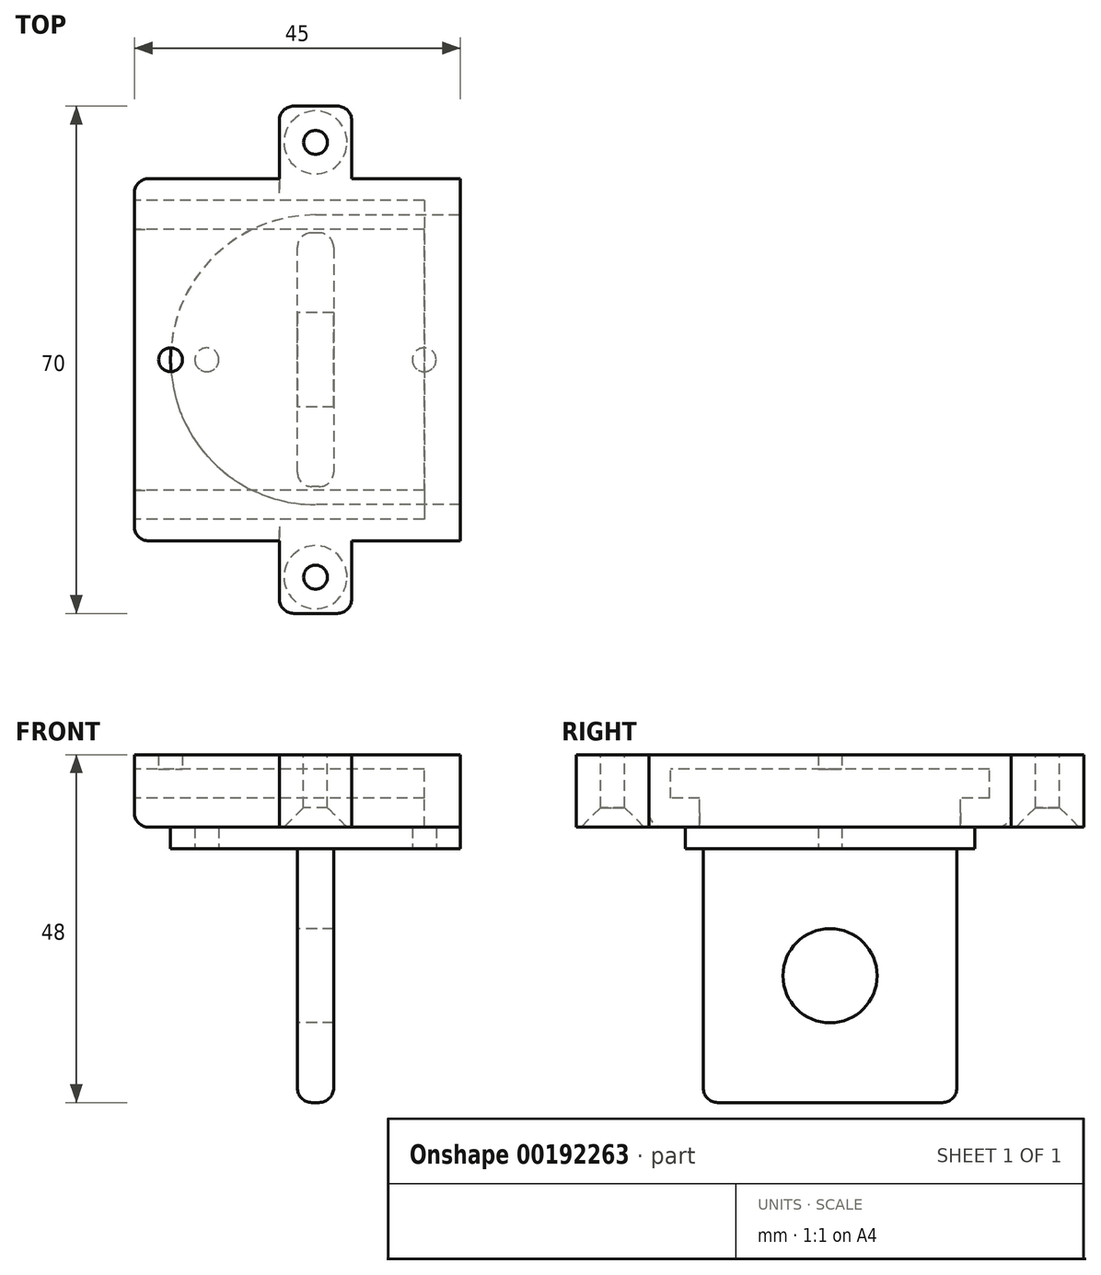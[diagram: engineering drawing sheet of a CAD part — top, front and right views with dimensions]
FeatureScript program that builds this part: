
annotation { "Feature Type Name" : "Feature", "Feature Type Description" : "" }
export const myFeature = defineFeature(function(context is Context, id is Id, definition is map)
    precondition{}
    {
        {
            var Q0;
            Q0=qCreatedBy(makeId("Right.planeOp"),FACE);
            var sketch = newSketch(context, id + "F0", { "sketchPlane" : qUnion([Q0])});
            skLineSegment(sketch, "E0", {"start": v(0, 0) * mm, "end": v(0, 35) * mm});
            skLineSegment(sketch, "E1", {"start": v(0, 35) * mm, "end": v(35, 35) * mm});
            skLineSegment(sketch, "E2", {"start": v(35, 35) * mm, "end": v(35, 0) * mm});
            skLineSegment(sketch, "E3", {"start": v(35, 0) * mm, "end": v(0, 0) * mm});
            skLineSegment(sketch, "E4", {"start": v(17.5, 35) * mm, "end": v(17.5, 0) * mm});
            skCircle(sketch, "E5", {"center": v(17.5, 17.5) * mm, "radius": 6.5 * mm});
            skSolve(sketch);
        }
        {
            var Q0;
            Q0 = qSketchRegion(id + "F0", true);
            var Q1;
            {var subQ6=sQuery(id+"F0.wireOp",EDGE,"E2");Q1=makeQuery(id+"F0.imprint","IMPRINT",FACE,{"disambiguationData":[TD([[makeQuery(id+"F0.imprint","IMPRINT",EDGE,{"derivedFrom":subQ6}),-1.0]])]});}
            extrude(context, id + "F1", {"entities" : qUnion([Q0, Q1]), "depth" : 5 * mm});
        }
        {
            var Q0;
            Q0=makeQuery(id+"F1.opExtrude","SWEPT_FACE",FACE,{"disambiguationData":[OSD([sQuery(id+"F0.wireOp",EDGE,"E1")])]});
            var sketch = newSketch(context, id + "F2", { "sketchPlane" : qUnion([Q0])});
            skLineSegment(sketch, "E6", {"start": v(0, 17.5) * mm, "end": v(5, 17.5) * mm});
            skCircle(sketch, "E7", {"center": v(2.5, 17.5) * mm, "radius": 20 * mm});
            skLineSegment(sketch, "E8", {"start": v(2.5, 17.5) * mm, "end": v(-17.5, 17.5) * mm});
            skLineSegment(sketch, "E9", {"start": v(-17.5, 17.5) * mm, "end": v(-17.5, 37.5) * mm});
            skLineSegment(sketch, "E10", {"start": v(-17.5, 37.5) * mm, "end": v(2.5, 37.5) * mm});
            skLineSegment(sketch, "E11", {"start": v(2.5, 37.5) * mm, "end": v(22.5, 37.5) * mm});
            skLineSegment(sketch, "E12", {"start": v(22.5, 37.5) * mm, "end": v(22.5, -2.5) * mm});
            skLineSegment(sketch, "E13", {"start": v(22.5, -2.5) * mm, "end": v(-17.5, -2.5) * mm});
            skLineSegment(sketch, "E14", {"start": v(-17.5, -2.5) * mm, "end": v(-17.5, 17.5) * mm});
            skSolve(sketch);
        }
        {
            var Q0;
            Q0=makeQuery(id+"F2.imprint","IMPRINT",FACE,{"disambiguationData":[TD([[makeQuery(id+"F2.imprint","IMPRINT",EDGE,{"derivedFrom":sQuery(id+"F2.wireOp",EDGE,"E7")}),1.0]])]});
            var Q1;
            {var subQ0=sQuery(id+"F2.wireOp",EDGE,"E6");Q1=makeQuery(id+"F2.imprint","IMPRINT",FACE,{"disambiguationData":[TD([[makeQuery(id+"F2.imprint","IMPRINT",EDGE,{"derivedFrom":subQ0}),1.0]])]});}
            var Q2;
            {var subQ0=sQuery(id+"F2.wireOp",EDGE,"E6");Q2=makeQuery(id+"F2.imprint","IMPRINT",FACE,{"disambiguationData":[TD([[makeQuery(id+"F2.imprint","IMPRINT",EDGE,{"derivedFrom":subQ0}),-1.0]])]});}
            var Q3;
            {var subQ0=sQuery(id+"F2.wireOp",EDGE,"E11");Q3=makeQuery(id+"F2.imprint","IMPRINT",FACE,{"disambiguationData":[TD([[makeQuery(id+"F2.imprint","IMPRINT",EDGE,{"derivedFrom":subQ0}),-1.0]])]});}
            var Q4;
            {var subQ0=sQuery(id+"F2.wireOp",EDGE,"E12");var subQ1=sQuery(id+"F2.wireOp",EDGE,"E7");var subQ2=makeQuery(id+"F2.imprint","INTERSECT",VERTEX,{"derivedFrom":[subQ1,subQ0]});Q4=makeQuery(id+"F2.imprint","IMPRINT",FACE,{"disambiguationData":[TD([[makeQuery(id+"F2.imprint","IMPRINT",EDGE,{"disambiguationData":[TD([[subQ2,1.0]])],"derivedFrom":subQ1}),-1.0]])]});}
            extrude(context, id + "F3", {"entities" : qUnion([Q0, Q1, Q2, Q3, Q4]), "operationType" : NewBodyOperationType.ADD, "depth" : 3 * mm});
        }
        {
            var Q0;
            Q0=makeQuery(id+"F3.opExtrude","CAP_FACE",FACE,{"disambiguationData":[OSD([sQuery(id+"F2.wireOp",EDGE,"E7")])],"isStart":false});
            var sketch = newSketch(context, id + "F4", { "sketchPlane" : qUnion([Q0])});
            skLineSegment(sketch, "E15", {"start": v(2.5, 17.5) * mm, "end": v(-17.5, 17.5) * mm});
            skLineSegment(sketch, "E16", {"start": v(-17.5, 17.5) * mm, "end": v(-12.5, 17.5) * mm});
            skLineSegment(sketch, "E17", {"start": v(2.5, 17.5) * mm, "end": v(2.5, 32.5) * mm});
            skLineSegment(sketch, "E18", {"start": v(2.5, 17.5) * mm, "end": v(17.5, 17.5) * mm});
            skSolve(sketch);
        }
        {
            var Q0;
            Q0=sQuery(id+"F4.wireOp",VERTEX,"E16.end");
            var Q1;
            Q1=sQuery(id+"F4.wireOp",VERTEX,"E18.end");
            var Q2;
            Q2=makeQuery(id+"F1.opExtrude","SWEPT_BODY",BODY,{"disambiguationData":[OSD([sQuery(id+"F0.wireOp",EDGE,"E0"),sQuery(id+"F0.wireOp",EDGE,"E1"),sQuery(id+"F0.wireOp",EDGE,"E2"),sQuery(id+"F0.wireOp",EDGE,"E3"),sQuery(id+"F0.wireOp",EDGE,"E5")])]});
            hole(context, id + "F5", {"style" : HoleStyle.SIMPLE, "endStyle" : HoleEndStyle.THROUGH, "holeDiameter" : 3.3 * mm, "locations" : qUnion([Q0, Q1]), "scope" : qUnion([Q2]), "isTappedThrough" : true, "startStyle" : HoleStartStyle.PART});
        }
        {
            var Q0;
            Q0=makeQuery(id+"F3.opExtrude","CAP_FACE",FACE,{"disambiguationData":[OSD([sQuery(id+"F2.wireOp",EDGE,"E7")])],"isStart":false});
            var sketch = newSketch(context, id + "F6", { "sketchPlane" : qUnion([Q0])});
            skLineSegment(sketch, "E19", {"start": v(2.5, 17.5) * mm, "end": v(2.5, 42.5) * mm});
            skLineSegment(sketch, "E20", {"start": v(2.5, 42.5) * mm, "end": v(22.5, 42.5) * mm});
            skLineSegment(sketch, "E21", {"start": v(22.5, 42.5) * mm, "end": v(22.5, -7.5) * mm});
            skLineSegment(sketch, "E22", {"start": v(22.5, -7.5) * mm, "end": v(-22.5, -7.5) * mm});
            skLineSegment(sketch, "E23", {"start": v(-22.5, -7.5) * mm, "end": v(-22.5, 42.5) * mm});
            skLineSegment(sketch, "E24", {"start": v(-22.5, 42.5) * mm, "end": v(2.5, 42.5) * mm});
            skLineSegment(sketch, "E25", {"start": v(2.5, 42.5) * mm, "end": v(-2.5, 42.5) * mm});
            skLineSegment(sketch, "E26", {"start": v(2.5, 17.5) * mm, "end": v(4.5, 17.5) * mm});
            skLineSegment(sketch, "E27.MirrorCS", {"start": v(5.33, -17.5) * mm, "end": v(5.33, -7.5) * mm});
            skLineSegment(sketch, "E28", {"start": v(-2.5, 42.5) * mm, "end": v(-2.5, 52.5) * mm});
            skLineSegment(sketch, "E29", {"start": v(-2.5, 52.5) * mm, "end": v(7.5, 52.5) * mm});
            skLineSegment(sketch, "E30", {"start": v(7.5, 52.5) * mm, "end": v(7.5, 42.5) * mm});
            skLineSegment(sketch, "E31.MirrorCS", {"start": v(-2.5, -17.5) * mm, "end": v(7.5, -17.5) * mm});
            skLineSegment(sketch, "E32.MirrorCS", {"start": v(7.5, -17.5) * mm, "end": v(7.5, -7.5) * mm});
            skLineSegment(sketch, "E33.MirrorCS", {"start": v(-2.5, -7.5) * mm, "end": v(-2.5, -17.5) * mm});
            skSolve(sketch);
        }
        {
            var Q0;
            Q0 = qSketchRegion(id + "F6", true);
            extrude(context, id + "F7", {"entities" : qUnion([Q0]), "depth" : 10 * mm});
        }
        {
            var Q0;
            Q0=makeQuery(id+"F7.opExtrude","SWEPT_FACE",FACE,{"disambiguationData":[OSD([sQuery(id+"F6.wireOp",EDGE,"E23")])]});
            var sketch = newSketch(context, id + "F8", { "sketchPlane" : qUnion([Q0])});
            skLineSegment(sketch, "E34", {"start": v(-42.5, 38) * mm, "end": v(-42.5, 42) * mm});
            skLineSegment(sketch, "E35", {"start": v(-42.5, 42) * mm, "end": v(7.5, 42) * mm});
            skPoint(sketch, "E35.endSnap0", {"position": v(7.5, 43) * mm});
            skLineSegment(sketch, "E36", {"start": v(7.5, 42) * mm, "end": v(7.5, 48) * mm});
            skLineSegment(sketch, "E37", {"start": v(7.5, 48) * mm, "end": v(-42.5, 48) * mm});
            skLineSegment(sketch, "E38", {"start": v(-42.5, 48) * mm, "end": v(-42.5, 42) * mm});
            skLineSegment(sketch, "E39", {"start": v(-42.5, 42) * mm, "end": v(-39.5, 42) * mm});
            skLineSegment(sketch, "E40", {"start": v(7.5, 42) * mm, "end": v(4.5, 42) * mm});
            skLineSegment(sketch, "E41", {"start": v(4.5, 42) * mm, "end": v(4.5, 48) * mm});
            skLineSegment(sketch, "E42", {"start": v(-39.5, 42) * mm, "end": v(-39.5, 48) * mm});
            skLineSegment(sketch, "E43", {"start": v(-17.5, 38) * mm, "end": v(-35.5, 38) * mm});
            skLineSegment(sketch, "E44", {"start": v(-35.5, 38) * mm, "end": v(0.5, 38) * mm});
            skLineSegment(sketch, "E45", {"start": v(0.5, 38) * mm, "end": v(0.5, 42) * mm});
            skLineSegment(sketch, "E46", {"start": v(-35.5, 38) * mm, "end": v(-35.5, 42) * mm});
            skLineSegment(sketch, "E47", {"start": v(-42.5, 48) * mm, "end": v(-42.5, 46) * mm});
            skLineSegment(sketch, "E48", {"start": v(-42.5, 46) * mm, "end": v(7.5, 46) * mm});
            skSolve(sketch);
        }
        {
            var Q0;
            Q0=makeQuery(id+"F8.imprint","IMPRINT",FACE,{"disambiguationData":[TD([[makeQuery(id+"F8.imprint","IMPRINT",EDGE,{"derivedFrom":sQuery(id+"F8.wireOp",EDGE,"E35")}),1.0]])]});
            var Q1;
            {var subQ0=sQuery(id+"F8.wireOp",EDGE,"E45");Q1=makeQuery(id+"F8.imprint","IMPRINT",FACE,{"disambiguationData":[TD([[makeQuery(id+"F8.imprint","IMPRINT",EDGE,{"derivedFrom":subQ0}),1.0]])]});}
            extrude(context, id + "F9", {"entities" : qUnion([Q0, Q1]), "operationType" : NewBodyOperationType.REMOVE, "oppositeDirection" : true, "depth" : 40 * mm});
        }
        {
            var Q0;
            Q0=makeQuery(id+"F7.opExtrude","CAP_FACE",FACE,{"disambiguationData":[OSD([sQuery(id+"F6.wireOp",EDGE,"E20"),sQuery(id+"F6.wireOp",EDGE,"E21"),sQuery(id+"F6.wireOp",EDGE,"E22"),sQuery(id+"F6.wireOp",EDGE,"E23"),sQuery(id+"F6.wireOp",EDGE,"E24"),sQuery(id+"F6.wireOp",EDGE,"E28"),sQuery(id+"F6.wireOp",EDGE,"E29"),sQuery(id+"F6.wireOp",EDGE,"E30"),sQuery(id+"F6.wireOp",EDGE,"E31.MirrorCS"),sQuery(id+"F6.wireOp",EDGE,"E32.MirrorCS"),sQuery(id+"F6.wireOp",EDGE,"E33.MirrorCS")])],"isStart":false});
            var sketch = newSketch(context, id + "F10", { "sketchPlane" : qUnion([Q0])});
            skLineSegment(sketch, "E49", {"start": v(-22.5, 17.5) * mm, "end": v(-17.5, 17.5) * mm});
            skCircle(sketch, "E50", {"center": v(-17.5, 17.5) * mm, "radius": 1.65 * mm});
            skSolve(sketch);
        }
        {
            var Q0;
            Q0=sQuery(id+"F10.wireOp",VERTEX,"E50.center");
            var Q1;
            Q1=makeQuery(id+"F1.opExtrude","SWEPT_BODY",BODY,{"disambiguationData":[OSD([sQuery(id+"F0.wireOp",EDGE,"E0"),sQuery(id+"F0.wireOp",EDGE,"E1"),sQuery(id+"F0.wireOp",EDGE,"E2"),sQuery(id+"F0.wireOp",EDGE,"E3"),sQuery(id+"F0.wireOp",EDGE,"E5")])]});
            var Q2;
            Q2=makeQuery(id+"F7.opExtrude","SWEPT_BODY",BODY,{"disambiguationData":[OSD([sQuery(id+"F6.wireOp",EDGE,"E20"),sQuery(id+"F6.wireOp",EDGE,"E21"),sQuery(id+"F6.wireOp",EDGE,"E22"),sQuery(id+"F6.wireOp",EDGE,"E23"),sQuery(id+"F6.wireOp",EDGE,"E24"),sQuery(id+"F6.wireOp",EDGE,"E28"),sQuery(id+"F6.wireOp",EDGE,"E29"),sQuery(id+"F6.wireOp",EDGE,"E30"),sQuery(id+"F6.wireOp",EDGE,"E31.MirrorCS"),sQuery(id+"F6.wireOp",EDGE,"E32.MirrorCS"),sQuery(id+"F6.wireOp",EDGE,"E33.MirrorCS")])]});
            hole(context, id + "F11", {"style" : HoleStyle.SIMPLE, "endStyle" : HoleEndStyle.BLIND, "holeDiameter" : 3.3 * mm, "holeDepth" : 5 * mm, "locations" : qUnion([Q0]), "scope" : qUnion([Q1, Q2]), "startStyle" : HoleStartStyle.PART});
        }
        {
            var Q0;
            Q0=makeQuery(id+"F1.opExtrude","SWEPT_FACE",FACE,{"disambiguationData":[OSD([sQuery(id+"F0.wireOp",EDGE,"E3")])]});
            var Q1;
            Q1=makeQuery(id+"F1.opExtrude","CAP_EDGE",EDGE,{"disambiguationData":[OSD([sQuery(id+"F0.wireOp",EDGE,"E0")])],"isStart":true});
            var Q2;
            Q2=makeQuery(id+"F1.opExtrude","CAP_EDGE",EDGE,{"disambiguationData":[OSD([sQuery(id+"F0.wireOp",EDGE,"E0")])],"isStart":false});
            var Q3;
            Q3=makeQuery(id+"F1.opExtrude","CAP_EDGE",EDGE,{"disambiguationData":[OSD([sQuery(id+"F0.wireOp",EDGE,"E2")])],"isStart":true});
            var Q4;
            Q4=makeQuery(id+"F1.opExtrude","CAP_EDGE",EDGE,{"disambiguationData":[OSD([sQuery(id+"F0.wireOp",EDGE,"E2")])],"isStart":false});
            fillet(context, id + "F12", {"entities" : qUnion([Q0, Q1, Q2, Q3, Q4]), "radius" : 2 * mm, "tangentPropagation" : true, "allowEdgeOverflow" : false});
        }
        {
            var Q0;
            Q0=makeQuery(id+"F7.opExtrude","CAP_FACE",FACE,{"disambiguationData":[OSD([sQuery(id+"F6.wireOp",EDGE,"E20"),sQuery(id+"F6.wireOp",EDGE,"E21"),sQuery(id+"F6.wireOp",EDGE,"E22"),sQuery(id+"F6.wireOp",EDGE,"E23"),sQuery(id+"F6.wireOp",EDGE,"E24"),sQuery(id+"F6.wireOp",EDGE,"E28"),sQuery(id+"F6.wireOp",EDGE,"E29"),sQuery(id+"F6.wireOp",EDGE,"E30"),sQuery(id+"F6.wireOp",EDGE,"E31.MirrorCS"),sQuery(id+"F6.wireOp",EDGE,"E32.MirrorCS"),sQuery(id+"F6.wireOp",EDGE,"E33.MirrorCS")])],"isStart":true});
            var sketch = newSketch(context, id + "F13", { "sketchPlane" : qUnion([Q0])});
            skLineSegment(sketch, "E51", {"start": v(-2.5, 12.5) * mm, "end": v(7.5, 12.5) * mm});
            skLineSegment(sketch, "E52", {"start": v(-2.5, -47.5) * mm, "end": v(7.5, -47.5) * mm});
            skLineSegment(sketch, "E53", {"start": v(2.5, 12.5) * mm, "end": v(2.5, 17.5) * mm});
            skLineSegment(sketch, "E54", {"start": v(2.5, -47.5) * mm, "end": v(2.5, -52.5) * mm});
            skSolve(sketch);
        }
        {
            var Q0;
            Q0=sQuery(id+"F13.wireOp",VERTEX,"E53.start");
            var Q1;
            Q1=sQuery(id+"F13.wireOp",VERTEX,"E54.start");
            var Q2;
            Q2=makeQuery(id+"F7.opExtrude","SWEPT_BODY",BODY,{"disambiguationData":[OSD([sQuery(id+"F6.wireOp",EDGE,"E20"),sQuery(id+"F6.wireOp",EDGE,"E21"),sQuery(id+"F6.wireOp",EDGE,"E22"),sQuery(id+"F6.wireOp",EDGE,"E23"),sQuery(id+"F6.wireOp",EDGE,"E24"),sQuery(id+"F6.wireOp",EDGE,"E28"),sQuery(id+"F6.wireOp",EDGE,"E29"),sQuery(id+"F6.wireOp",EDGE,"E30"),sQuery(id+"F6.wireOp",EDGE,"E31.MirrorCS"),sQuery(id+"F6.wireOp",EDGE,"E32.MirrorCS"),sQuery(id+"F6.wireOp",EDGE,"E33.MirrorCS")])]});
            hole(context, id + "F14", {"style" : HoleStyle.C_SINK, "endStyle" : HoleEndStyle.BLIND, "holeDiameter" : 3.3 * mm, "cSinkDiameter" : 8.7 * mm, "cSinkAngle" : 90 * degree, "holeDepth" : 10 * mm, "locations" : qUnion([Q0, Q1]), "scope" : qUnion([Q2]), "startStyle" : HoleStartStyle.PART});
        }
        {
            var Q0;
            {var subQ0=sQuery(id+"F6.wireOp",EDGE,"E24");var subQ1=sQuery(id+"F6.wireOp",EDGE,"E23");Q0=makeQuery(id+"F9.boolean.opBoolean","SPLIT",EDGE,{"disambiguationData":[TD([makeQuery(id+"F7.opExtrude","SWEPT_FACE",FACE,{"disambiguationData":[OSD([subQ0])]})])],"derivedFrom":makeQuery(id+"F7.opExtrude","CAP_EDGE",EDGE,{"disambiguationData":[OSD([subQ1])],"isStart":true})});}
            var Q1;
            {var subQ1=sQuery(id+"F6.wireOp",EDGE,"E23");Q1=makeQuery(id+"F9.boolean.opBoolean","SPLIT",EDGE,{"disambiguationData":[TD([makeQuery(id+"F9.opExtrude","SWEPT_FACE",FACE,{"disambiguationData":[OSD([sQuery(id+"F8.wireOp",EDGE,"E45")])]})])],"derivedFrom":makeQuery(id+"F7.opExtrude","CAP_EDGE",EDGE,{"disambiguationData":[OSD([subQ1])],"isStart":true})});}
            var Q2;
            Q2=makeQuery(id+"F7.opExtrude","SWEPT_EDGE",EDGE,{"disambiguationData":[OSD([sQuery(id+"F6.wireOp",EDGE,"E22"),sQuery(id+"F6.wireOp",EDGE,"E23")])]});
            var Q3;
            Q3=makeQuery(id+"F7.opExtrude","SWEPT_EDGE",EDGE,{"disambiguationData":[OSD([sQuery(id+"F6.wireOp",EDGE,"E23"),sQuery(id+"F6.wireOp",EDGE,"E24")])]});
            var Q4;
            {var subQ0=sQuery(id+"F6.wireOp",EDGE,"E22");Q4=makeQuery(id+"F7.opExtrude","CAP_EDGE",EDGE,{"disambiguationData":[OSD([subQ0]),TDD([makeQuery(id+"F6.imprint","IMPRINT",EDGE,{"disambiguationData":[TD([[makeQuery(id+"F6.imprint","INTERSECT",VERTEX,{"derivedFrom":[subQ0,sQuery(id+"F6.wireOp",EDGE,"E23")]}),1.0]])],"derivedFrom":subQ0})])],"isStart":true});}
            var Q5;
            Q5=makeQuery(id+"F7.opExtrude","CAP_EDGE",EDGE,{"disambiguationData":[OSD([sQuery(id+"F6.wireOp",EDGE,"E24")])],"isStart":true});
            var Q6;
            Q6=makeQuery(id+"F7.opExtrude","SWEPT_EDGE",EDGE,{"disambiguationData":[OSD([sQuery(id+"F6.wireOp",EDGE,"E28"),sQuery(id+"F6.wireOp",EDGE,"E29")])]});
            var Q7;
            Q7=makeQuery(id+"F7.opExtrude","SWEPT_EDGE",EDGE,{"disambiguationData":[OSD([sQuery(id+"F6.wireOp",EDGE,"E31.MirrorCS"),sQuery(id+"F6.wireOp",EDGE,"E33.MirrorCS")])]});
            var Q8;
            Q8=makeQuery(id+"F7.opExtrude","SWEPT_EDGE",EDGE,{"disambiguationData":[OSD([sQuery(id+"F6.wireOp",EDGE,"E31.MirrorCS"),sQuery(id+"F6.wireOp",EDGE,"E32.MirrorCS")])]});
            var Q9;
            Q9=makeQuery(id+"F7.opExtrude","SWEPT_EDGE",EDGE,{"disambiguationData":[OSD([sQuery(id+"F6.wireOp",EDGE,"E29"),sQuery(id+"F6.wireOp",EDGE,"E30")])]});
            fillet(context, id + "F15", {"entities" : qUnion([Q0, Q1, Q2, Q3, Q4, Q5, Q6, Q7, Q8, Q9]), "radius" : 2 * mm, "tangentPropagation" : true, "allowEdgeOverflow" : false});
        }
    });
